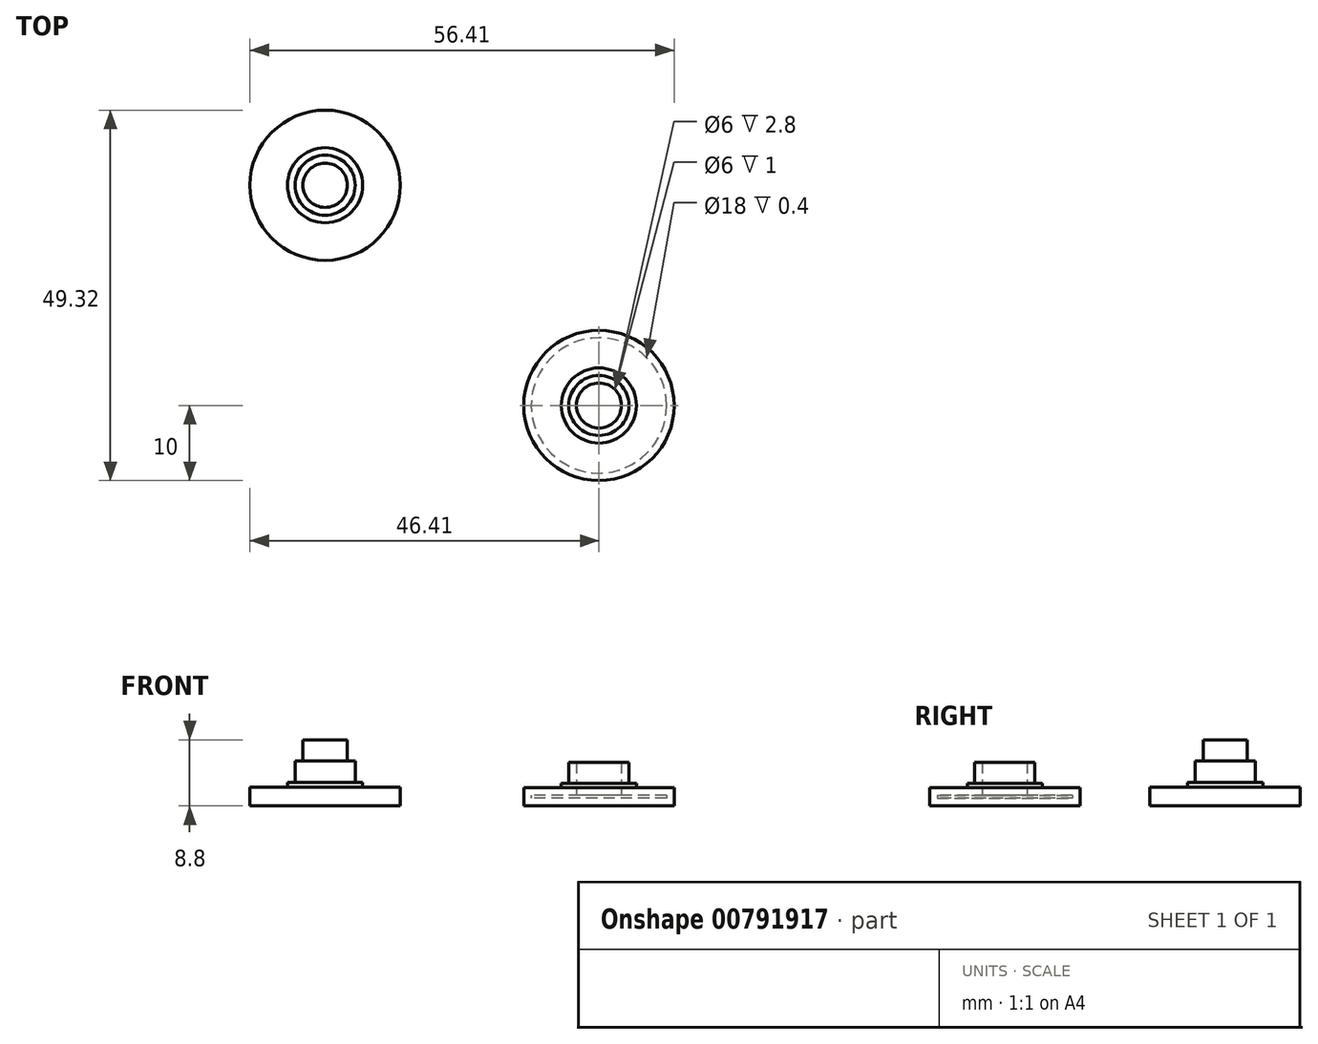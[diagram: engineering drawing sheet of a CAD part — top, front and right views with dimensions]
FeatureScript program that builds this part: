
annotation { "Feature Type Name" : "Feature", "Feature Type Description" : "" }
export const myFeature = defineFeature(function(context is Context, id is Id, definition is map)
    precondition{}
    {
        {
            var Q0;
            Q0=qCreatedBy(makeId("Top.planeOp"),FACE);
            var sketch = newSketch(context, id + "F0", { "sketchPlane" : qUnion([Q0])});
            skCircle(sketch, "E0", {"center": v(0, 0) * mm, "radius": 10 * mm});
            skSolve(sketch);
        }
        {
            var Q0;
            Q0=makeQuery(id+"F0.imprint","IMPRINT",FACE,{"disambiguationData":[TD([[makeQuery(id+"F0.imprint","IMPRINT",EDGE,{"derivedFrom":sQuery(id+"F0.wireOp",EDGE,"E0")}),1.0]])]});
            extrude(context, id + "F1", {"entities" : qUnion([Q0]), "depth" : 2.4 * mm, "offsetDistance" : 25 * mm});
        }
        {
            var Q0;
            Q0=makeQuery(id+"F1.opExtrude","CAP_FACE",FACE,{"disambiguationData":[OSD([sQuery(id+"F0.wireOp",EDGE,"E0")])],"isStart":false});
            var sketch = newSketch(context, id + "F2", { "sketchPlane" : qUnion([Q0])});
            skCircle(sketch, "E1", {"center": v(0, 0) * mm, "radius": 4 * mm});
            skSolve(sketch);
        }
        {
            var Q0;
            Q0=makeQuery(id+"F2.imprint","IMPRINT",FACE,{"disambiguationData":[TD([[makeQuery(id+"F2.imprint","IMPRINT",EDGE,{"derivedFrom":sQuery(id+"F2.wireOp",EDGE,"E1")}),1.0]])]});
            extrude(context, id + "F3", {"entities" : qUnion([Q0]), "operationType" : NewBodyOperationType.ADD, "depth" : 3.4 * mm, "offsetDistance" : 25 * mm});
        }
        {
            var Q0;
            Q0=makeQuery(id+"F3.opExtrude","CAP_FACE",FACE,{"disambiguationData":[OSD([sQuery(id+"F2.wireOp",EDGE,"E1")])],"isStart":false});
            shell(context, id + "F4", {"entities" : qUnion([Q0]), "thickness" : 1 * mm});
        }
        {
            var Q0;
            Q0=makeQuery(id+"F1.opExtrude","CAP_FACE",FACE,{"disambiguationData":[OSD([sQuery(id+"F0.wireOp",EDGE,"E0")])],"isStart":false});
            var sketch = newSketch(context, id + "F5", { "sketchPlane" : qUnion([Q0])});
            skCircle(sketch, "E2", {"center": v(0, 0) * mm, "radius": 5 * mm});
            skSolve(sketch);
        }
        {
            var Q0;
            Q0=qSketchRegion(id+"F5",true);
            extrude(context, id + "F6", {"entities" : qUnion([Q0]), "operationType" : NewBodyOperationType.ADD, "depth" : .6 * mm, "offsetDistance" : 25 * mm});
        }
        {
            var Q0;
            Q0=qCreatedBy(makeId("Top.planeOp"),FACE);
            var sketch = newSketch(context, id + "F7", { "sketchPlane" : qUnion([Q0])});
            skCircle(sketch, "E3", {"center": v(-36.41, 29.32) * mm, "radius": 10 * mm});
            skSolve(sketch);
        }
        {
            var Q0;
            Q0=makeQuery(id+"F7.imprint","IMPRINT",FACE,{"disambiguationData":[TD([[makeQuery(id+"F7.imprint","IMPRINT",EDGE,{"derivedFrom":sQuery(id+"F7.wireOp",EDGE,"E3")}),1.0]])]});
            extrude(context, id + "F8", {"entities" : qUnion([Q0]), "depth" : 2.5 * mm, "offsetDistance" : 25 * mm});
        }
        {
            var Q0;
            Q0=makeQuery(id+"F8.opExtrude","CAP_FACE",FACE,{"disambiguationData":[OSD([sQuery(id+"F7.wireOp",EDGE,"E3")])],"isStart":false});
            var sketch = newSketch(context, id + "F9", { "sketchPlane" : qUnion([Q0])});
            skCircle(sketch, "E4", {"center": v(-36.41, 29.32) * mm, "radius": 4 * mm});
            skSolve(sketch);
        }
        {
            var Q0;
            Q0=makeQuery(id+"F9.imprint","IMPRINT",FACE,{"disambiguationData":[TD([[makeQuery(id+"F9.imprint","IMPRINT",EDGE,{"derivedFrom":sQuery(id+"F9.wireOp",EDGE,"E4")}),1.0]])]});
            extrude(context, id + "F10", {"entities" : qUnion([Q0]), "operationType" : NewBodyOperationType.ADD, "depth" : 3.5 * mm, "offsetDistance" : 25 * mm});
        }
        {
            var Q0;
            Q0=makeQuery(id+"F10.opExtrude","CAP_FACE",FACE,{"disambiguationData":[OSD([sQuery(id+"F9.wireOp",EDGE,"E4")])],"isStart":false});
            var sketch = newSketch(context, id + "F11", { "sketchPlane" : qUnion([Q0])});
            skCircle(sketch, "E5", {"center": v(-36.41, 29.32) * mm, "radius": 2.95 * mm});
            skSolve(sketch);
        }
        {
            var Q0;
            Q0=qSketchRegion(id+"F11",true);
            extrude(context, id + "F12", {"entities" : qUnion([Q0]), "operationType" : NewBodyOperationType.ADD, "depth" : 2.8 * mm, "offsetDistance" : 25 * mm});
        }
        {
            var Q0;
            Q0=makeQuery(id+"F8.opExtrude","CAP_FACE",FACE,{"disambiguationData":[OSD([sQuery(id+"F7.wireOp",EDGE,"E3")])],"isStart":false});
            var sketch = newSketch(context, id + "F13", { "sketchPlane" : qUnion([Q0])});
            skCircle(sketch, "E6", {"center": v(-36.41, 29.32) * mm, "radius": 5 * mm});
            skSolve(sketch);
        }
        {
            var Q0;
            Q0=makeQuery(id+"F13.imprint","IMPRINT",FACE,{"disambiguationData":[TD([[makeQuery(id+"F13.imprint","IMPRINT",EDGE,{"derivedFrom":sQuery(id+"F13.wireOp",EDGE,"E6")}),1.0]])]});
            var Q1;
            Q1 = qSketchRegion(id + "F11", true);
            var Q2;
            Q2 = qSketchRegion(id + "F9", true);
            var Q3;
            Q3 = qSketchRegion(id + "F7", true);
            extrude(context, id + "F14", {"entities" : qUnion([Q0, Q1, Q2, Q3]), "operationType" : NewBodyOperationType.ADD, "depth" : .6 * mm, "offsetDistance" : 25 * mm});
        }
    });
